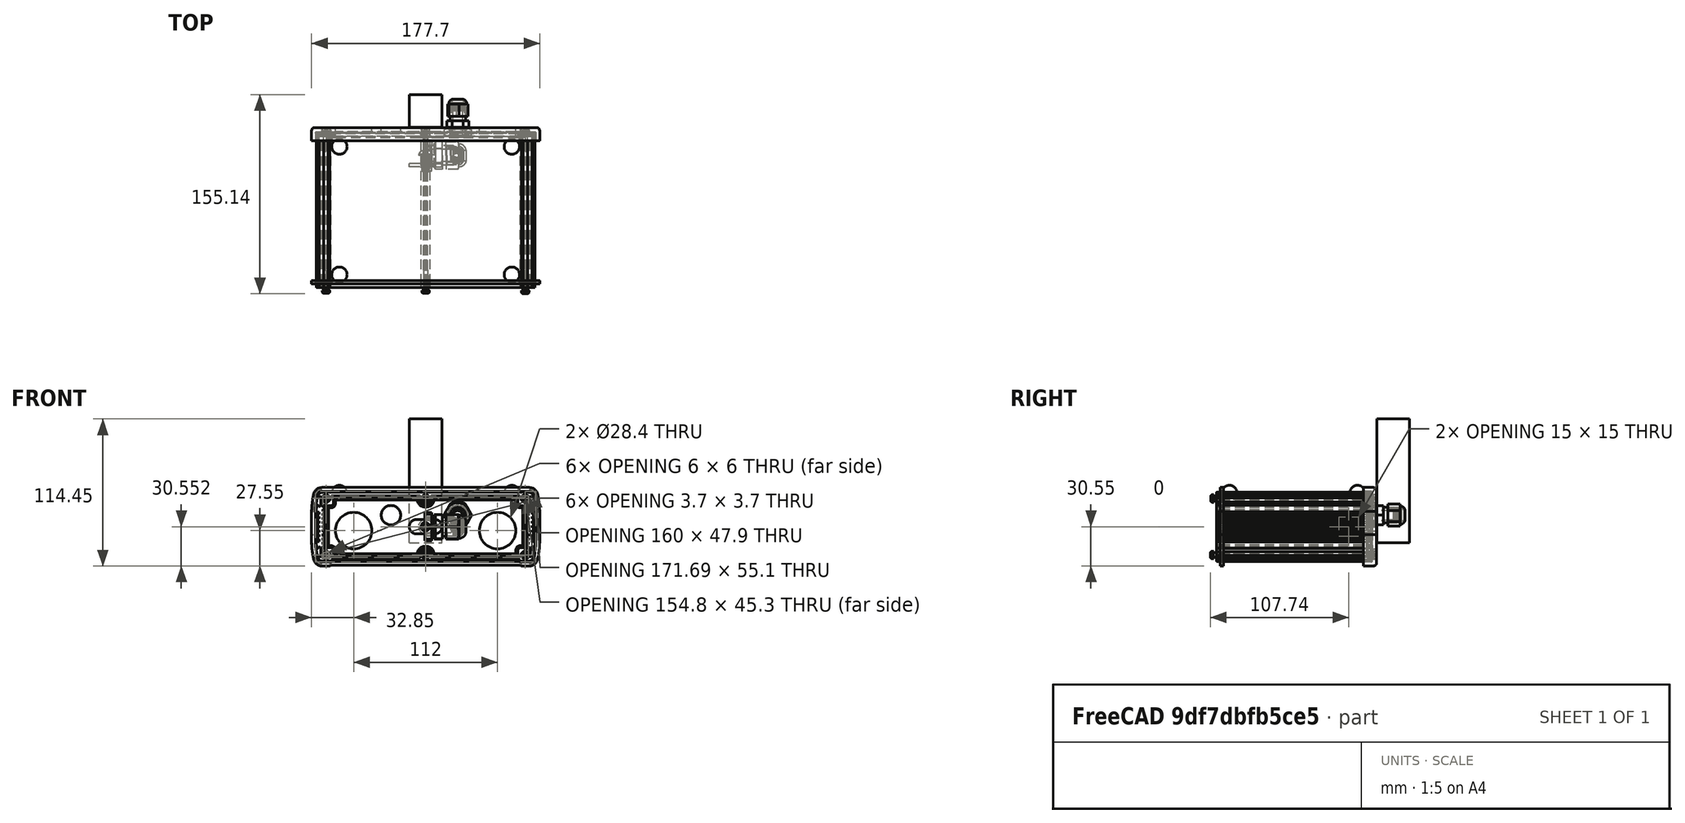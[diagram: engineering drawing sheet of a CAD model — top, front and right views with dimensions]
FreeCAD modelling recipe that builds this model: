
FCSTD DOCUMENT  (FreeCAD 0.19R24276 (Git))
Label: polyCaseCutOuts-2
License: All rights reserved
LicenseURL: http://en.wikipedia.org/wiki/All_rights_reserved
objects: TechDraw::DrawViewDimension×50, Part::Feature×28, Part::Cylinder×10, Part::Compound2×4, Part::Cut×4, Part::Box×3, Part::MultiFuse×2, TechDraw::DrawViewPart×2, TechDraw::DrawPage×2, TechDraw::DrawSVGTemplate×1
note: 47 computed .brp shape members not serialized (recipe doc carries the construction recipe); baked Part::Feature solids carry a one-line shape summary decoded from their .brp

FEATURE [Part::Feature] Feature  label="EX-64-002"
  Placement = pos=(0,-43,1e-14) rot=(0,0.707107,-0.707107;3.14159rad)
  shape: bbox 178.8 x 129.6 x 63.35 mm, 1628 faces, 33 solids (baked)
FEATURE [Part::Feature] Shell020
  shape: bbox 36.98 x 18.12 x 36.6 mm, 205 faces, 0 solids (baked)
FEATURE [Part::Feature] Shell021
  shape: bbox 36.98 x 21.68 x 36.68 mm, 152 faces, 0 solids (baked)
FEATURE [Part::Feature] Shell022
  shape: bbox 22.66 x 11.43 x 22.66 mm, 6 faces, 0 solids (baked)
FEATURE [Part::Feature] Shell023
  shape: bbox 24.46 x 14.2 x 24.46 mm, 102 faces, 0 solids (baked)
FEATURE [Part::Feature] Shell024
  shape: bbox 35.58 x 29.16 x 35.58 mm, 49 faces, 0 solids (baked)
FEATURE [Part::Feature] Shell025
  shape: bbox 0.2577 x 0.3048 x 0.4459 mm, 1 faces, 0 solids (baked)
FEATURE [Part::Feature] Shell026
  shape: bbox 0.3892 x 1.194 x 0.6742 mm, 1 faces, 0 solids (baked)
FEATURE [Part::Feature] Shell027
  shape: bbox 0.3612 x 0.889 x 0.6255 mm, 1 faces, 0 solids (baked)
FEATURE [Part::Feature] Shell028
  shape: bbox 0.2703 x 0.381 x 0.4682 mm, 1 faces, 0 solids (baked)
FEATURE [Part::Compound2] Compound001  label="M3222GBH_SW0001"
  Links = -> [Shell020,Shell021,Shell022,Shell023,Shell024,Shell025,Shell026,Shell027,Shell028]
  Placement = pos=(-56,9,-3) rot=(0,0,1;0rad)
FEATURE [Part::Feature] Solid003
  shape: bbox 15.45 x 36 x 21.9 mm, 27 faces (baked)
FEATURE [Part::Feature] Solid004
  shape: bbox 29.5 x 21.9 x 19 mm, 79 faces (baked)
FEATURE [Part::Feature] Solid002
  shape: bbox 1 x 19 x 19 mm, 6 faces (baked)
FEATURE [Part::Feature] Solid005
  shape: bbox 5.2 x 24 x 22.95 mm, 27 faces (baked)
FEATURE [Part::Feature] Solid001
  shape: bbox 8 x 12 x 12 mm, 6 faces (baked)
FEATURE [Part::Compound2] Compound002  label="PG9"
  Links = -> [Solid004,Solid001,Solid002,Solid003,Solid005]
  Placement = pos=(-27,14,9) rot=(0,0,1;1.5708rad)
FEATURE [Part::Box] Box  label="tSlotLog"
  AttacherType = Attacher::AttachEngine3D
  Height = 96.4
  Length = 25.4
  Placement = pos=(-12.7,22,-12.5) rot=(0,0,1;0rad)
  Width = 25.4
FEATURE [Part::Feature] Feature001  label="PG7"
  Placement = pos=(25,27,9) rot=(1,0,0;1.5708rad)
  shape: bbox 21.32 x 29.79 x 20.97 mm, 246 faces, 3 solids (baked)
FEATURE [Part::Feature] Shell029
  shape: bbox 36.98 x 21.68 x 36.68 mm, 152 faces, 0 solids (baked)
FEATURE [Part::Feature] Shell030
  shape: bbox 22.66 x 11.43 x 22.66 mm, 6 faces, 0 solids (baked)
FEATURE [Part::Feature] Shell031
  shape: bbox 0.3612 x 0.889 x 0.6255 mm, 1 faces, 0 solids (baked)
FEATURE [Part::Feature] Shell032
  shape: bbox 35.58 x 29.16 x 35.58 mm, 49 faces, 0 solids (baked)
FEATURE [Part::Feature] Shell033
  shape: bbox 24.46 x 14.2 x 24.46 mm, 102 faces, 0 solids (baked)
FEATURE [Part::Feature] Shell034
  shape: bbox 0.3892 x 1.194 x 0.6742 mm, 1 faces, 0 solids (baked)
FEATURE [Part::Feature] Shell035
  shape: bbox 0.2703 x 0.381 x 0.4682 mm, 1 faces, 0 solids (baked)
FEATURE [Part::Feature] Shell036
  shape: bbox 0.2577 x 0.3048 x 0.4459 mm, 1 faces, 0 solids (baked)
FEATURE [Part::Feature] Shell037
  shape: bbox 36.98 x 18.12 x 36.6 mm, 205 faces, 0 solids (baked)
FEATURE [Part::Compound2] Compound003  label="M3222GBH_SW0002"
  Links = -> [Shell037,Shell029,Shell030,Shell033,Shell032,Shell036,Shell034,Shell031,Shell035]
  Placement = pos=(56,9,-3) rot=(0,0,1;0rad)
FEATURE [Part::Feature] Solid
  shape: bbox 11.1 x 17.44 x 11.1 mm, 45 faces (baked)
FEATURE [Part::Feature] Solid006
  shape: bbox 25.4 x 3.15 x 11.25 mm, 11 faces (baked)
FEATURE [Part::Compound2] Compound  label="47065T139_T-Slotted Framing"
  Links = -> [Solid,Solid006]
  Placement = pos=(-2.4e-15,15,0) rot=(-0.707107,0,0.707107;3.14159rad)
FEATURE [Part::Cylinder] Cylinder  label="tSlotCut"
  Angle = 360
  AttacherType = Attacher::AttachEngine3D
  Height = 20
  Placement = pos=(0,9,0) rot=(-1,0,0;1.5708rad)
  Radius = 3.2
FEATURE [Part::Cylinder] Cylinder001  label="M3222GBH_SW0001_Cut"
  Angle = 360
  AttacherType = Attacher::AttachEngine3D
  Height = 50
  Placement = pos=(-56,-5,-3) rot=(-1,0,0;1.5708rad)
  Radius = 14.2
FEATURE [Part::Cylinder] Cylinder002  label="M3222GBH_SW0001_Cut001"
  Angle = 360
  AttacherType = Attacher::AttachEngine3D
  Height = 50
  Placement = pos=(56,-5,-3) rot=(-1,0,0;1.5708rad)
  Radius = 14.2
FEATURE [Part::Cylinder] Cylinder003  label="PG9Cut"
  Angle = 360
  AttacherType = Attacher::AttachEngine3D
  Height = 20
  Placement = pos=(-27,9,9) rot=(-1,0,0;1.5708rad)
  Radius = 7.6
FEATURE [Part::Cylinder] Cylinder004  label="PG9Cut001"
  Angle = 360
  AttacherType = Attacher::AttachEngine3D
  Height = 20
  Placement = pos=(25,9,9) rot=(-1,0,0;1.5708rad)
  Radius = 6.2
FEATURE [Part::MultiFuse] Fusion  label="cuts"
  Shapes = -> [Cylinder004,Cylinder003,Cylinder,Cylinder001,Cylinder002]
FEATURE [Part::Cut] Cut  label="Ex-64Cuts"
  Base = -> Feature
  Tool = -> Fusion
FEATURE [TechDraw::DrawViewPart] View  label="External View"
  CoarseView = false
  Direction = (0,1,0)
  Focus = 100
  HardHidden = false
  IsoCount = 0
  IsoHidden = false
  IsoVisible = false
  LockPosition = false
  Perspective = false
  Rotation = 0
  ScaleType = 0
  SeamHidden = false
  SeamVisible = true
  SmoothHidden = false
  SmoothVisible = true
  Source = -> [Cut]
  X = 101.612
  XDirection = (-1,0,0)
  Y = 166.066
FEATURE [TechDraw::DrawViewDimension] Dimension002
  Arbitrary = false
  ArbitraryTolerances = false
  EqualTolerance = true
  FormatSpec = ⌀%.2f
  FormatSpecOverTolerance = %+.2f
  FormatSpecUnderTolerance = %+.2f
  Inverted = false
  LockPosition = false
  MeasureType = 1
  OverTolerance = 0
  References2D = -> [View]
  Rotation = 0
  ScaleType = 0
  TheoreticalExact = false
  Type = 5
  UnderTolerance = 0
  X = -26.8003
  Y = 11.2115
FEATURE [TechDraw::DrawViewDimension] Dimension001
  Arbitrary = false
  ArbitraryTolerances = false
  EqualTolerance = true
  FormatSpec = ⌀%.2f
  FormatSpecOverTolerance = %+.2f
  FormatSpecUnderTolerance = %+.2f
  Inverted = false
  LockPosition = false
  MeasureType = 1
  OverTolerance = 0
  References2D = -> [View]
  Rotation = 0
  ScaleType = 0
  TheoreticalExact = false
  Type = 5
  UnderTolerance = 0
  X = -53.3802
  Y = 0.342317
FEATURE [TechDraw::DrawViewDimension] Dimension
  Arbitrary = false
  ArbitraryTolerances = false
  EqualTolerance = true
  FormatSpec = %.2f
  FormatSpecOverTolerance = %+.2f
  FormatSpecUnderTolerance = %+.2f
  Inverted = false
  LockPosition = false
  MeasureType = 1
  OverTolerance = 0
  References2D = -> [View]
  Rotation = 0
  ScaleType = 0
  TheoreticalExact = false
  Type = 1
  UnderTolerance = 0
  X = 7.11e-14
  Y = -30.5235
FEATURE [TechDraw::DrawViewDimension] Dimension004
  Arbitrary = false
  ArbitraryTolerances = false
  EqualTolerance = true
  FormatSpec = ⌀%.2f
  FormatSpecOverTolerance = %+.2f
  FormatSpecUnderTolerance = %+.2f
  Inverted = false
  LockPosition = false
  MeasureType = 1
  OverTolerance = 0
  References2D = -> [View]
  Rotation = 0
  ScaleType = 0
  TheoreticalExact = false
  Type = 5
  UnderTolerance = 0
  X = 29.4596
  Y = 12.3737
FEATURE [TechDraw::DrawViewDimension] Dimension005
  Arbitrary = false
  ArbitraryTolerances = false
  EqualTolerance = true
  FormatSpec = ⌀%.2f
  FormatSpecOverTolerance = %+.2f
  FormatSpecUnderTolerance = %+.2f
  Inverted = false
  LockPosition = false
  MeasureType = 1
  OverTolerance = 0
  References2D = -> [View]
  Rotation = 0
  ScaleType = 0
  TheoreticalExact = false
  Type = 5
  UnderTolerance = 0
  X = 60.4786
  Y = 0.493887
FEATURE [TechDraw::DrawViewDimension] Dimension009
  Arbitrary = false
  ArbitraryTolerances = false
  EqualTolerance = true
  FormatSpec = %.2f
  FormatSpecOverTolerance = %+.2f
  FormatSpecUnderTolerance = %+.2f
  Inverted = false
  LockPosition = false
  MeasureType = 1
  OverTolerance = 0
  References2D = -> [View]
  Rotation = 0
  ScaleType = 0
  TheoreticalExact = false
  Type = 2
  UnderTolerance = 0
  X = -59.3059
  Y = 20.4711
FEATURE [TechDraw::DrawViewDimension] Dimension003
  Arbitrary = false
  ArbitraryTolerances = false
  EqualTolerance = true
  FormatSpec = ⌀%.2f
  FormatSpecOverTolerance = %+.2f
  FormatSpecUnderTolerance = %+.2f
  Inverted = false
  LockPosition = false
  MeasureType = 1
  OverTolerance = 0
  References2D = -> [View]
  Rotation = 0
  ScaleType = 0
  TheoreticalExact = false
  Type = 5
  UnderTolerance = 0
  X = 8.56795
  Y = 3.56177
FEATURE [TechDraw::DrawViewDimension] Dimension010
  Arbitrary = false
  ArbitraryTolerances = false
  EqualTolerance = true
  FormatSpec = %.2f
  FormatSpecOverTolerance = %+.2f
  FormatSpecUnderTolerance = %+.2f
  Inverted = false
  LockPosition = false
  MeasureType = 1
  OverTolerance = 0
  References2D = -> [View]
  Rotation = 0
  ScaleType = 0
  TheoreticalExact = false
  Type = 1
  UnderTolerance = 0
  X = -79.7934
  Y = 0.297386
FEATURE [TechDraw::DrawViewDimension] Dimension011
  Arbitrary = false
  ArbitraryTolerances = false
  EqualTolerance = true
  FormatSpec = %.2f
  FormatSpecOverTolerance = %+.2f
  FormatSpecUnderTolerance = %+.2f
  Inverted = false
  LockPosition = false
  MeasureType = 1
  OverTolerance = 0
  References2D = -> [View]
  Rotation = 0
  ScaleType = 0
  TheoreticalExact = false
  Type = 2
  UnderTolerance = 0
  X = -57.5045
  Y = -22.196
FEATURE [TechDraw::DrawViewDimension] Dimension012
  Arbitrary = false
  ArbitraryTolerances = false
  EqualTolerance = true
  FormatSpec = %.2f
  FormatSpecOverTolerance = %+.2f
  FormatSpecUnderTolerance = %+.2f
  Inverted = false
  LockPosition = false
  MeasureType = 1
  OverTolerance = 0
  References2D = -> [View]
  Rotation = 0
  ScaleType = 0
  TheoreticalExact = false
  Type = 2
  UnderTolerance = 0
  X = -26.9248
  Y = 24.0346
FEATURE [TechDraw::DrawViewDimension] Dimension013
  Arbitrary = false
  ArbitraryTolerances = false
  EqualTolerance = true
  FormatSpec = %.2f
  FormatSpecOverTolerance = %+.2f
  FormatSpecUnderTolerance = %+.2f
  Inverted = false
  LockPosition = false
  MeasureType = 1
  OverTolerance = 0
  References2D = -> [View]
  Rotation = 0
  ScaleType = 0
  TheoreticalExact = false
  Type = 2
  UnderTolerance = 0
  X = 22.4977
  Y = 25.2623
FEATURE [TechDraw::DrawViewDimension] Dimension014
  Arbitrary = false
  ArbitraryTolerances = false
  EqualTolerance = true
  FormatSpec = %.2f
  FormatSpecOverTolerance = %+.2f
  FormatSpecUnderTolerance = %+.2f
  Inverted = false
  LockPosition = false
  MeasureType = 1
  OverTolerance = 0
  References2D = -> [View]
  Rotation = 0
  ScaleType = 0
  TheoreticalExact = false
  Type = 2
  UnderTolerance = 0
  X = 52.8053
  Y = 21.0418
FEATURE [TechDraw::DrawViewDimension] Dimension015
  Arbitrary = false
  ArbitraryTolerances = false
  EqualTolerance = true
  FormatSpec = %.2f
  FormatSpecOverTolerance = %+.2f
  FormatSpecUnderTolerance = %+.2f
  Inverted = false
  LockPosition = false
  MeasureType = 1
  OverTolerance = 0
  References2D = -> [View]
  Rotation = 0
  ScaleType = 0
  TheoreticalExact = false
  Type = 1
  UnderTolerance = 0
  X = 78.3597
  Y = 2.50131
FEATURE [TechDraw::DrawViewDimension] Dimension016
  Arbitrary = false
  ArbitraryTolerances = false
  EqualTolerance = true
  FormatSpec = %.2f
  FormatSpecOverTolerance = %+.2f
  FormatSpecUnderTolerance = %+.2f
  Inverted = false
  LockPosition = false
  MeasureType = 1
  OverTolerance = 0
  References2D = -> [View]
  Rotation = 0
  ScaleType = 0
  TheoreticalExact = false
  Type = 2
  UnderTolerance = 0
  X = 53.3164
  Y = -21.4677
FEATURE [TechDraw::DrawViewDimension] Dimension017
  Arbitrary = false
  ArbitraryTolerances = false
  EqualTolerance = true
  FormatSpec = %.2f
  FormatSpecOverTolerance = %+.2f
  FormatSpecUnderTolerance = %+.2f
  Inverted = false
  LockPosition = false
  MeasureType = 1
  OverTolerance = 0
  References2D = -> [View]
  Rotation = 0
  ScaleType = 0
  TheoreticalExact = false
  Type = 1
  UnderTolerance = 0
  X = -60.9532
  Y = 5.48366
FEATURE [TechDraw::DrawViewDimension] Dimension018
  Arbitrary = false
  ArbitraryTolerances = false
  EqualTolerance = true
  FormatSpec = %.2f
  FormatSpecOverTolerance = %+.2f
  FormatSpecUnderTolerance = %+.2f
  Inverted = false
  LockPosition = false
  MeasureType = 1
  OverTolerance = 0
  References2D = -> [View]
  Rotation = 0
  ScaleType = 0
  TheoreticalExact = false
  Type = 1
  UnderTolerance = 0
  X = 17.0933
  Y = -2.49522
FEATURE [TechDraw::DrawViewDimension] Dimension019
  Arbitrary = false
  ArbitraryTolerances = false
  EqualTolerance = true
  FormatSpec = %.2f
  FormatSpecOverTolerance = %+.2f
  FormatSpecUnderTolerance = %+.2f
  Inverted = false
  LockPosition = false
  MeasureType = 1
  OverTolerance = 0
  References2D = -> [View]
  Rotation = 0
  ScaleType = 0
  TheoreticalExact = false
  Type = 2
  UnderTolerance = 0
  X = -28.1319
  Y = -12.4515
FEATURE [TechDraw::DrawViewDimension] Dimension020
  Arbitrary = false
  ArbitraryTolerances = false
  EqualTolerance = true
  FormatSpec = %.2f
  FormatSpecOverTolerance = %+.2f
  FormatSpecUnderTolerance = %+.2f
  Inverted = false
  LockPosition = false
  MeasureType = 1
  OverTolerance = 0
  References2D = -> [View]
  Rotation = 0
  ScaleType = 0
  TheoreticalExact = false
  Type = 1
  UnderTolerance = 0
  X = 25.0729
  Y = -6.69401
FEATURE [TechDraw::DrawViewDimension] Dimension021
  Arbitrary = false
  ArbitraryTolerances = false
  EqualTolerance = true
  FormatSpec = %.2f
  FormatSpecOverTolerance = %+.2f
  FormatSpecUnderTolerance = %+.2f
  Inverted = false
  LockPosition = false
  MeasureType = 1
  OverTolerance = 0
  References2D = -> [View]
  Rotation = 0
  ScaleType = 0
  TheoreticalExact = false
  Type = 2
  UnderTolerance = 0
  X = -6.99932
  Y = -13.6516
FEATURE [TechDraw::DrawViewDimension] Dimension022
  Arbitrary = false
  ArbitraryTolerances = false
  EqualTolerance = true
  FormatSpec = %.2f
  FormatSpecOverTolerance = %+.2f
  FormatSpecUnderTolerance = %+.2f
  Inverted = false
  LockPosition = false
  MeasureType = 1
  OverTolerance = 0
  References2D = -> [View]
  Rotation = 0
  ScaleType = 0
  TheoreticalExact = false
  Type = 2
  UnderTolerance = 0
  X = -9.15587
  Y = 20.4863
FEATURE [TechDraw::DrawViewDimension] Dimension023
  Arbitrary = false
  ArbitraryTolerances = false
  EqualTolerance = true
  FormatSpec = %.2f
  FormatSpecOverTolerance = %+.2f
  FormatSpecUnderTolerance = %+.2f
  Inverted = false
  LockPosition = false
  MeasureType = 1
  OverTolerance = 0
  References2D = -> [View]
  Rotation = 0
  ScaleType = 0
  TheoreticalExact = false
  Type = 1
  UnderTolerance = 0
  X = -43.0308
  Y = 9.91992
FEATURE [TechDraw::DrawViewDimension] Dimension024
  Arbitrary = false
  ArbitraryTolerances = false
  EqualTolerance = true
  FormatSpec = %.2f
  FormatSpecOverTolerance = %+.2f
  FormatSpecUnderTolerance = %+.2f
  Inverted = false
  LockPosition = false
  MeasureType = 1
  OverTolerance = 0
  References2D = -> [View]
  Rotation = 0
  ScaleType = 0
  TheoreticalExact = false
  Type = 1
  UnderTolerance = 0
  X = -41.9951
  Y = 17.0467
FEATURE [TechDraw::DrawViewDimension] Dimension025
  Arbitrary = false
  ArbitraryTolerances = false
  EqualTolerance = true
  FormatSpec = %.2f
  FormatSpecOverTolerance = %+.2f
  FormatSpecUnderTolerance = %+.2f
  Inverted = false
  LockPosition = false
  MeasureType = 1
  OverTolerance = 0
  References2D = -> [View]
  Rotation = 0
  ScaleType = 0
  TheoreticalExact = false
  Type = 1
  UnderTolerance = 0
  X = -42.6156
  Y = 23.097
FEATURE [TechDraw::DrawViewDimension] Dimension026
  Arbitrary = false
  ArbitraryTolerances = false
  EqualTolerance = true
  FormatSpec = %.2f
  FormatSpecOverTolerance = %+.2f
  FormatSpecUnderTolerance = %+.2f
  Inverted = false
  LockPosition = false
  MeasureType = 1
  OverTolerance = 0
  References2D = -> [View]
  Rotation = 0
  ScaleType = 0
  TheoreticalExact = false
  Type = 1
  UnderTolerance = 0
  X = 28.9388
  Y = -11.288
FEATURE [TechDraw::DrawViewDimension] Dimension027
  Arbitrary = false
  ArbitraryTolerances = false
  EqualTolerance = true
  FormatSpec = %.2f
  FormatSpecOverTolerance = %+.2f
  FormatSpecUnderTolerance = %+.2f
  Inverted = false
  LockPosition = false
  MeasureType = 1
  OverTolerance = 0
  References2D = -> [View]
  Rotation = 0
  ScaleType = 0
  TheoreticalExact = false
  Type = 1
  UnderTolerance = 0
  X = 73.1961
  Y = 10.1708
FEATURE [Part::Box] Box001  label="Cube"
  AttacherType = Attacher::AttachEngine3D
  Height = 100
  Length = 300
  Placement = pos=(-130,-136,-46) rot=(0,0,1;0rad)
  Width = 36
FEATURE [Part::Cut] Cut001
  Base = -> Cut
  Tool = -> Box001
FEATURE [TechDraw::DrawViewPart] View001  label="InternalView"
  CoarseView = false
  Direction = (0,-1,0)
  Focus = 100
  HardHidden = false
  IsoCount = 0
  IsoHidden = false
  IsoVisible = false
  LockPosition = false
  Perspective = false
  Rotation = 0
  ScaleType = 0
  SeamHidden = false
  SeamVisible = true
  SmoothHidden = false
  SmoothVisible = true
  Source = -> [Cut001]
  X = 113.858
  XDirection = (1,0,0)
  Y = 93.139
FEATURE [TechDraw::DrawViewDimension] Dimension028
  Arbitrary = false
  ArbitraryTolerances = false
  EqualTolerance = true
  FormatSpec = ⌀%.2f
  FormatSpecOverTolerance = %+.2f
  FormatSpecUnderTolerance = %+.2f
  Inverted = false
  LockPosition = false
  MeasureType = 1
  OverTolerance = 0
  References2D = -> [View001]
  Rotation = 0
  ScaleType = 0
  TheoreticalExact = false
  Type = 5
  UnderTolerance = 0
  X = -63.861
  Y = -0.6213
FEATURE [Part::Feature] Feature002  label="EX-64-003"
  Placement = pos=(0,-43,1e-14) rot=(0,0.707107,-0.707107;3.14159rad)
  shape: bbox 178.8 x 129.6 x 63.35 mm, 1628 faces, 33 solids (baked)
FEATURE [Part::Cylinder] Cylinder005  label="tSlotCut001"
  Angle = 360
  AttacherType = Attacher::AttachEngine3D
  Height = 20
  Placement = pos=(0,9,0) rot=(-1,0,0;1.5708rad)
  Radius = 3.2
FEATURE [Part::Cylinder] Cylinder006  label="M3222GBH_SW0001_Cut002"
  Angle = 360
  AttacherType = Attacher::AttachEngine3D
  Height = 50
  Placement = pos=(-56,-5,-3) rot=(-1,0,0;1.5708rad)
  Radius = 14.2
FEATURE [Part::Cylinder] Cylinder007  label="M3222GBH_SW0001_Cut003"
  Angle = 360
  AttacherType = Attacher::AttachEngine3D
  Height = 50
  Placement = pos=(56,-5,-3) rot=(-1,0,0;1.5708rad)
  Radius = 14.2
FEATURE [Part::Cylinder] Cylinder008  label="PG9Cut002"
  Angle = 360
  AttacherType = Attacher::AttachEngine3D
  Height = 20
  Placement = pos=(-27,9,9) rot=(-1,0,0;1.5708rad)
  Radius = 7.6
FEATURE [Part::Cylinder] Cylinder009  label="PG9Cut003"
  Angle = 360
  AttacherType = Attacher::AttachEngine3D
  Height = 20
  Placement = pos=(25,9,9) rot=(-1,0,0;1.5708rad)
  Radius = 6.2
FEATURE [Part::MultiFuse] Fusion001  label="cuts001"
  Shapes = -> [Cylinder009,Cylinder008,Cylinder005,Cylinder006,Cylinder007]
FEATURE [Part::Cut] Cut002  label="Ex-64Cuts001"
  Base = -> Feature002
  Tool = -> Fusion001
FEATURE [Part::Box] Box002  label="Cube001"
  AttacherType = Attacher::AttachEngine3D
  Height = 100
  Length = 300
  Placement = pos=(-130,-136,-46) rot=(0,0,1;0rad)
  Width = 36
FEATURE [Part::Cut] Cut003
  Base = -> Cut002
  Tool = -> Box002
FEATURE [TechDraw::DrawSVGTemplate] Template
  EditableTexts = Designed_by_Name=Lakitha Wijeratne; Drawing_number=0.1; FC-Date=04/27/2022; FC-SC=1:1; FC-Title=UTD LoRaWAN Node
  Height = 210
  Orientation = 1
  Width = 297
FEATURE [TechDraw::DrawPage] Page001
  KeepUpdated = true
  NextBalloonIndex = 1
  ProjectionType = 0
  Template = -> Template
FEATURE [TechDraw::DrawViewDimension] Dimension029
  Arbitrary = false
  ArbitraryTolerances = false
  EqualTolerance = true
  FormatSpec = ⌀%.2f
  FormatSpecOverTolerance = %+.2f
  FormatSpecUnderTolerance = %+.2f
  Inverted = false
  LockPosition = false
  MeasureType = 1
  OverTolerance = 0
  References2D = -> [View001]
  Rotation = 0
  ScaleType = 0
  TheoreticalExact = false
  Type = 5
  UnderTolerance = 0
  X = -26.0935
  Y = 13.2914
FEATURE [TechDraw::DrawViewDimension] Dimension030
  Arbitrary = false
  ArbitraryTolerances = false
  EqualTolerance = true
  FormatSpec = ⌀%.2f
  FormatSpecOverTolerance = %+.2f
  FormatSpecUnderTolerance = %+.2f
  Inverted = false
  LockPosition = false
  MeasureType = 1
  OverTolerance = 0
  References2D = -> [View001]
  Rotation = 0
  ScaleType = 0
  TheoreticalExact = false
  Type = 5
  UnderTolerance = 0
  X = 8.29158
  Y = 3.19129
FEATURE [TechDraw::DrawViewDimension] Dimension031
  Arbitrary = false
  ArbitraryTolerances = false
  EqualTolerance = true
  FormatSpec = ⌀%.2f
  FormatSpecOverTolerance = %+.2f
  FormatSpecUnderTolerance = %+.2f
  Inverted = false
  LockPosition = false
  MeasureType = 1
  OverTolerance = 0
  References2D = -> [View001]
  Rotation = 0
  ScaleType = 0
  TheoreticalExact = false
  Type = 5
  UnderTolerance = 0
  X = 24.1164
  Y = 12.0582
FEATURE [TechDraw::DrawViewDimension] Dimension032
  Arbitrary = false
  ArbitraryTolerances = false
  EqualTolerance = true
  FormatSpec = ⌀%.2f
  FormatSpecOverTolerance = %+.2f
  FormatSpecUnderTolerance = %+.2f
  Inverted = false
  LockPosition = false
  MeasureType = 1
  OverTolerance = 0
  References2D = -> [View001]
  Rotation = 0
  ScaleType = 0
  TheoreticalExact = false
  Type = 5
  UnderTolerance = 0
  X = 58.1619
  Y = 1.79217
FEATURE [TechDraw::DrawViewDimension] Dimension033
  Arbitrary = false
  ArbitraryTolerances = false
  EqualTolerance = true
  FormatSpec = %.2f
  FormatSpecOverTolerance = %+.2f
  FormatSpecUnderTolerance = %+.2f
  Inverted = false
  LockPosition = false
  MeasureType = 1
  OverTolerance = 0
  References2D = -> [View001]
  Rotation = 0
  ScaleType = 0
  TheoreticalExact = false
  Type = 2
  UnderTolerance = 0
  X = -38.214
  Y = 12.6115
FEATURE [TechDraw::DrawViewDimension] Dimension034
  Arbitrary = false
  ArbitraryTolerances = false
  EqualTolerance = true
  FormatSpec = %.2f
  FormatSpecOverTolerance = %+.2f
  FormatSpecUnderTolerance = %+.2f
  Inverted = false
  LockPosition = false
  MeasureType = 1
  OverTolerance = 0
  References2D = -> [View001]
  Rotation = 0
  ScaleType = 0
  TheoreticalExact = false
  Type = 2
  UnderTolerance = 0
  X = -60.8676
  Y = 15.822
FEATURE [TechDraw::DrawViewDimension] Dimension036
  Arbitrary = false
  ArbitraryTolerances = false
  EqualTolerance = true
  FormatSpec = %.2f
  FormatSpecOverTolerance = %+.2f
  FormatSpecUnderTolerance = %+.2f
  Inverted = false
  LockPosition = false
  MeasureType = 1
  OverTolerance = 0
  References2D = -> [View001]
  Rotation = 0
  ScaleType = 0
  TheoreticalExact = false
  Type = 2
  UnderTolerance = 0
  X = -1.98752
  Y = 8.94686
FEATURE [TechDraw::DrawViewDimension] Dimension037
  Arbitrary = false
  ArbitraryTolerances = false
  EqualTolerance = true
  FormatSpec = %.2f
  FormatSpecOverTolerance = %+.2f
  FormatSpecUnderTolerance = %+.2f
  Inverted = false
  LockPosition = false
  MeasureType = 1
  OverTolerance = 0
  References2D = -> [View001]
  Rotation = 0
  ScaleType = 0
  TheoreticalExact = false
  Type = 2
  UnderTolerance = 0
  X = 15.7334
  Y = 17.5719
FEATURE [TechDraw::DrawViewDimension] Dimension038
  Arbitrary = false
  ArbitraryTolerances = false
  EqualTolerance = true
  FormatSpec = %.2f
  FormatSpecOverTolerance = %+.2f
  FormatSpecUnderTolerance = %+.2f
  Inverted = false
  LockPosition = false
  MeasureType = 1
  OverTolerance = 0
  References2D = -> [View001]
  Rotation = 0
  ScaleType = 0
  TheoreticalExact = false
  Type = 2
  UnderTolerance = 0
  X = 47.0593
  Y = 16.115
FEATURE [TechDraw::DrawViewDimension] Dimension039
  Arbitrary = false
  ArbitraryTolerances = false
  EqualTolerance = true
  FormatSpec = %.2f
  FormatSpecOverTolerance = %+.2f
  FormatSpecUnderTolerance = %+.2f
  Inverted = false
  LockPosition = false
  MeasureType = 1
  OverTolerance = 0
  References2D = -> [View001]
  Rotation = 0
  ScaleType = 0
  TheoreticalExact = false
  Type = 2
  UnderTolerance = 0
  X = -39.4981
  Y = -10.4872
FEATURE [TechDraw::DrawViewDimension] Dimension040
  Arbitrary = false
  ArbitraryTolerances = false
  EqualTolerance = true
  FormatSpec = %.2f
  FormatSpecOverTolerance = %+.2f
  FormatSpecUnderTolerance = %+.2f
  Inverted = false
  LockPosition = false
  MeasureType = 1
  OverTolerance = 0
  References2D = -> [View001]
  Rotation = 0
  ScaleType = 0
  TheoreticalExact = false
  Type = 2
  UnderTolerance = 0
  X = -26.9239
  Y = -10.1041
FEATURE [TechDraw::DrawViewDimension] Dimension041
  Arbitrary = false
  ArbitraryTolerances = false
  EqualTolerance = true
  FormatSpec = %.2f
  FormatSpecOverTolerance = %+.2f
  FormatSpecUnderTolerance = %+.2f
  Inverted = false
  LockPosition = false
  MeasureType = 1
  OverTolerance = 0
  References2D = -> [View001]
  Rotation = 0
  ScaleType = 0
  TheoreticalExact = false
  Type = 2
  UnderTolerance = 0
  X = -1.1758
  Y = -9.62262
FEATURE [TechDraw::DrawViewDimension] Dimension042
  Arbitrary = false
  ArbitraryTolerances = false
  EqualTolerance = true
  FormatSpec = %.2f
  FormatSpecOverTolerance = %+.2f
  FormatSpecUnderTolerance = %+.2f
  Inverted = false
  LockPosition = false
  MeasureType = 1
  OverTolerance = 0
  References2D = -> [View001]
  Rotation = 0
  ScaleType = 0
  TheoreticalExact = false
  Type = 2
  UnderTolerance = 0
  X = 25.0761
  Y = -9.24762
FEATURE [TechDraw::DrawViewDimension] Dimension043
  Arbitrary = false
  ArbitraryTolerances = false
  EqualTolerance = true
  FormatSpec = %.2f
  FormatSpecOverTolerance = %+.2f
  FormatSpecUnderTolerance = %+.2f
  Inverted = false
  LockPosition = false
  MeasureType = 1
  OverTolerance = 0
  References2D = -> [View001]
  Rotation = 0
  ScaleType = 0
  TheoreticalExact = false
  Type = 2
  UnderTolerance = 0
  X = 38.2424
  Y = -10.4872
FEATURE [TechDraw::DrawViewDimension] Dimension044
  Arbitrary = false
  ArbitraryTolerances = false
  EqualTolerance = true
  FormatSpec = %.2f
  FormatSpecOverTolerance = %+.2f
  FormatSpecUnderTolerance = %+.2f
  Inverted = false
  LockPosition = false
  MeasureType = 1
  OverTolerance = 0
  References2D = -> [View001]
  Rotation = 0
  ScaleType = 0
  TheoreticalExact = false
  Type = 1
  UnderTolerance = 0
  X = -66.2295
  Y = 13.7874
FEATURE [TechDraw::DrawViewDimension] Dimension045
  Arbitrary = false
  ArbitraryTolerances = false
  EqualTolerance = true
  FormatSpec = %.2f
  FormatSpecOverTolerance = %+.2f
  FormatSpecUnderTolerance = %+.2f
  Inverted = false
  LockPosition = false
  MeasureType = 1
  OverTolerance = 0
  References2D = -> [View001]
  Rotation = 0
  ScaleType = 0
  TheoreticalExact = false
  Type = 1
  UnderTolerance = 0
  X = -50.868
  Y = 5.16015
FEATURE [TechDraw::DrawViewDimension] Dimension046
  Arbitrary = false
  ArbitraryTolerances = false
  EqualTolerance = true
  FormatSpec = %.2f
  FormatSpecOverTolerance = %+.2f
  FormatSpecUnderTolerance = %+.2f
  Inverted = false
  LockPosition = false
  MeasureType = 1
  OverTolerance = 0
  References2D = -> [View001]
  Rotation = 0
  ScaleType = 0
  TheoreticalExact = false
  Type = 1
  UnderTolerance = 0
  X = -17.6489
  Y = -0.469136
FEATURE [TechDraw::DrawViewDimension] Dimension047
  Arbitrary = false
  ArbitraryTolerances = false
  EqualTolerance = true
  FormatSpec = %.2f
  FormatSpecOverTolerance = %+.2f
  FormatSpecUnderTolerance = %+.2f
  Inverted = false
  LockPosition = false
  MeasureType = 1
  OverTolerance = 0
  References2D = -> [View001]
  Rotation = 0
  ScaleType = 0
  TheoreticalExact = false
  Type = 1
  UnderTolerance = 0
  X = -12.5295
  Y = 8.93505
FEATURE [TechDraw::DrawViewDimension] Dimension048
  Arbitrary = false
  ArbitraryTolerances = false
  EqualTolerance = true
  FormatSpec = %.2f
  FormatSpecOverTolerance = %+.2f
  FormatSpecUnderTolerance = %+.2f
  Inverted = false
  LockPosition = false
  MeasureType = 1
  OverTolerance = 0
  References2D = -> [View001]
  Rotation = 0
  ScaleType = 0
  TheoreticalExact = false
  Type = 1
  UnderTolerance = 0
  X = 14.3936
  Y = -2.55085
FEATURE [TechDraw::DrawViewDimension] Dimension049
  Arbitrary = false
  ArbitraryTolerances = false
  EqualTolerance = true
  FormatSpec = %.2f
  FormatSpecOverTolerance = %+.2f
  FormatSpecUnderTolerance = %+.2f
  Inverted = false
  LockPosition = false
  MeasureType = 1
  OverTolerance = 0
  References2D = -> [View001]
  Rotation = 0
  ScaleType = 0
  TheoreticalExact = false
  Type = 1
  UnderTolerance = 0
  X = 11.9527
  Y = -15.1814
FEATURE [TechDraw::DrawViewDimension] Dimension050
  Arbitrary = false
  ArbitraryTolerances = false
  EqualTolerance = true
  FormatSpec = %.2f
  FormatSpecOverTolerance = %+.2f
  FormatSpecUnderTolerance = %+.2f
  Inverted = false
  LockPosition = false
  MeasureType = 1
  OverTolerance = 0
  References2D = -> [View001]
  Rotation = 0
  ScaleType = 0
  TheoreticalExact = false
  Type = 1
  UnderTolerance = 0
  X = 54.0488
  Y = 7.11731
FEATURE [TechDraw::DrawViewDimension] Dimension051
  Arbitrary = false
  ArbitraryTolerances = false
  EqualTolerance = true
  FormatSpec = %.2f
  FormatSpecOverTolerance = %+.2f
  FormatSpecUnderTolerance = %+.2f
  Inverted = false
  LockPosition = false
  MeasureType = 1
  OverTolerance = 0
  References2D = -> [View001]
  Rotation = 0
  ScaleType = 0
  TheoreticalExact = false
  Type = 1
  UnderTolerance = 0
  X = 56.8752
  Y = -5.66322
FEATURE [TechDraw::DrawViewDimension] Dimension052
  Arbitrary = false
  ArbitraryTolerances = false
  EqualTolerance = true
  FormatSpec = %.2f
  FormatSpecOverTolerance = %+.2f
  FormatSpecUnderTolerance = %+.2f
  Inverted = false
  LockPosition = false
  MeasureType = 1
  OverTolerance = 0
  References2D = -> [View001]
  Rotation = 0
  ScaleType = 0
  TheoreticalExact = false
  Type = 1
  UnderTolerance = 0
  X = 64.915
  Y = 13.3018
FEATURE [TechDraw::DrawViewDimension] Dimension053
  Arbitrary = false
  ArbitraryTolerances = false
  EqualTolerance = true
  FormatSpec = %.2f
  FormatSpecOverTolerance = %+.2f
  FormatSpecUnderTolerance = %+.2f
  Inverted = false
  LockPosition = false
  MeasureType = 1
  OverTolerance = 0
  References2D = -> [View001]
  Rotation = 0
  ScaleType = 0
  TheoreticalExact = false
  Type = 1
  UnderTolerance = 0
  X = 61.1373
  Y = 19.8863
FEATURE [TechDraw::DrawPage] Page  label="CutOuts-Polycase"
  KeepUpdated = true
  NextBalloonIndex = 1
  ProjectionType = 0
  Template = -> Template
  Views = -> [View,Dimension,Dimension001,Dimension002,Dimension003,Dimension004,Dimension005,Dimension009,Dimension010,Dimension011,Dimension012,Dimension013,Dimension014,Dimension015,Dimension016,Dimension017,Dimension018,Dimension019,Dimension020,Dimension021,Dimension022,Dimension023,Dimension024,Dimension025,Dimension026,Dimension027,View001,Dimension028,Dimension029,Dimension030,Dimension031,Dimension032,+20 more]
